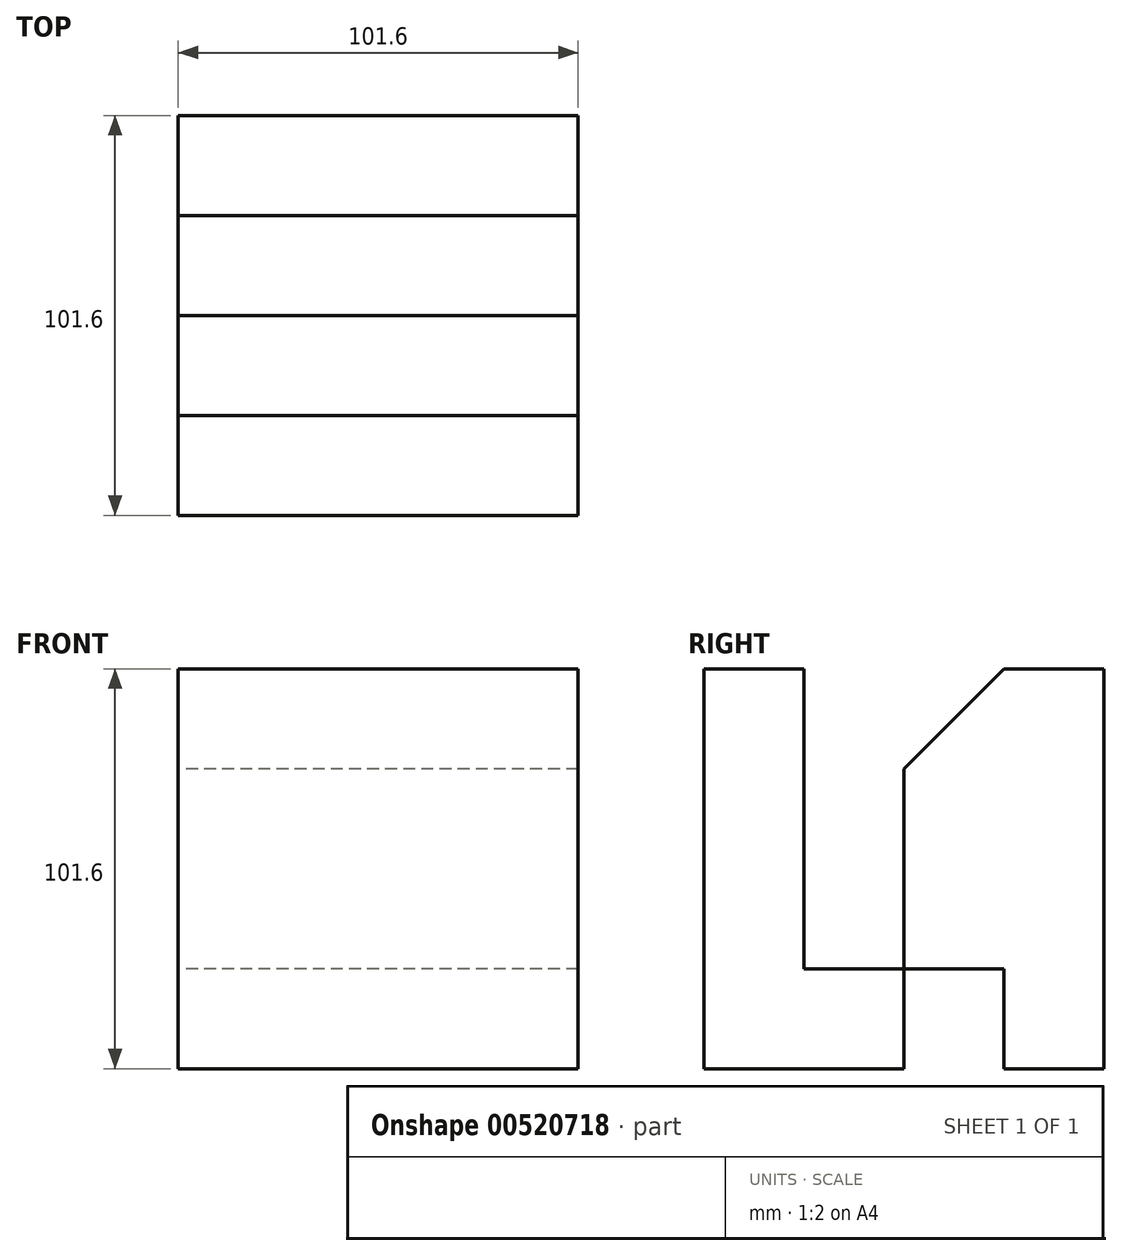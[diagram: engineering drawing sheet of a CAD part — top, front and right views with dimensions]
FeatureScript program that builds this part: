
annotation { "Feature Type Name" : "Feature", "Feature Type Description" : "" }
export const myFeature = defineFeature(function(context is Context, id is Id, definition is map)
    precondition{}
    {
        {
            var Q0;
            Q0=qCreatedBy(makeId("Top.planeOp"),FACE);
            var sketch = newSketch(context, id + "F0", { "sketchPlane" : qUnion([Q0])});
            skLineSegment(sketch, "E0.bottom", {"start": v(-50.8, -50.8) * mm, "end": v(50.8, -50.8) * mm});
            skLineSegment(sketch, "E0.top", {"start": v(-50.8, 50.8) * mm, "end": v(50.8, 50.8) * mm});
            skLineSegment(sketch, "E0.left", {"start": v(-50.8, -50.8) * mm, "end": v(-50.8, 50.8) * mm});
            skLineSegment(sketch, "E0.right", {"start": v(50.8, -50.8) * mm, "end": v(50.8, 50.8) * mm});
            skPoint(sketch, "E0.middle", {"position": v(0, 0) * mm});
            skSolve(sketch);
        }
        {
            var Q0;
            Q0 = qSketchRegion(id + "F0", true);
            extrude(context, id + "F1", {"entities" : qUnion([Q0]), "depth" : 101.6 * mm, "offsetDistance" : 25.4 * mm});
        }
        {
            var Q0;
            Q0=makeQuery(id+"F1.opExtrude","SWEPT_FACE",FACE,{"disambiguationData":[OSD([sQuery(id+"F0.wireOp",EDGE,"E0.left")])]});
            var sketch = newSketch(context, id + "F2", { "sketchPlane" : qUnion([Q0])});
            skLineSegment(sketch, "E1.bottom", {"start": v(-50.8, 101.6) * mm, "end": v(-25.4, 101.6) * mm});
            skLineSegment(sketch, "E1.top", {"start": v(-50.8, 0) * mm, "end": v(-25.4, 0) * mm});
            skLineSegment(sketch, "E1.left", {"start": v(-50.8, 101.6) * mm, "end": v(-50.8, 0) * mm});
            skLineSegment(sketch, "E1.right", {"start": v(-25.4, 101.6) * mm, "end": v(-25.4, 0) * mm});
            skLineSegment(sketch, "E2.bottom", {"start": v(50.8, 101.6) * mm, "end": v(25.4, 101.6) * mm});
            skLineSegment(sketch, "E2.top", {"start": v(50.8, 0) * mm, "end": v(25.4, 0) * mm});
            skLineSegment(sketch, "E2.left", {"start": v(50.8, 101.6) * mm, "end": v(50.8, 0) * mm});
            skLineSegment(sketch, "E2.right", {"start": v(25.4, 101.6) * mm, "end": v(25.4, 0) * mm});
            skLineSegment(sketch, "E3.bottom", {"start": v(-50.8, 101.6) * mm, "end": v(50.8, 101.6) * mm});
            skLineSegment(sketch, "E3.top", {"start": v(-50.8, 76.2) * mm, "end": v(50.8, 76.2) * mm});
            skLineSegment(sketch, "E3.left", {"start": v(-50.8, 101.6) * mm, "end": v(-50.8, 76.2) * mm});
            skLineSegment(sketch, "E3.right", {"start": v(50.8, 101.6) * mm, "end": v(50.8, 76.2) * mm});
            skLineSegment(sketch, "E4.bottom", {"start": v(50.8, 101.6) * mm, "end": v(0, 101.6) * mm});
            skLineSegment(sketch, "E4.top", {"start": v(50.8, 0) * mm, "end": v(0, 0) * mm});
            skLineSegment(sketch, "E4.right", {"start": v(0, 101.6) * mm, "end": v(0, 0) * mm});
            skLineSegment(sketch, "E5.bottom", {"start": v(-50.8, 0) * mm, "end": v(50.8, 0) * mm});
            skLineSegment(sketch, "E5.top", {"start": v(-50.8, 25.4) * mm, "end": v(50.8, 25.4) * mm});
            skLineSegment(sketch, "E5.left", {"start": v(-50.8, 0) * mm, "end": v(-50.8, 25.4) * mm});
            skLineSegment(sketch, "E5.right", {"start": v(50.8, 0) * mm, "end": v(50.8, 25.4) * mm});
            skLineSegment(sketch, "E6.bottom", {"start": v(50.8, 76.2) * mm, "end": v(38.1, 76.2) * mm});
            skLineSegment(sketch, "E6.top", {"start": v(50.8, 50.8) * mm, "end": v(38.1, 50.8) * mm});
            skLineSegment(sketch, "E6.left", {"start": v(50.8, 76.2) * mm, "end": v(50.8, 50.8) * mm});
            skLineSegment(sketch, "E6.right", {"start": v(38.1, 76.2) * mm, "end": v(38.1, 50.8) * mm});
            skLineSegment(sketch, "E7.bottom", {"start": v(-50.8, 76.2) * mm, "end": v(-38.1, 76.2) * mm});
            skLineSegment(sketch, "E7.top", {"start": v(-50.8, 44.75) * mm, "end": v(-38.1, 44.75) * mm});
            skLineSegment(sketch, "E7.left", {"start": v(-50.8, 76.2) * mm, "end": v(-50.8, 44.75) * mm});
            skLineSegment(sketch, "E7.right", {"start": v(-38.1, 76.2) * mm, "end": v(-38.1, 44.75) * mm});
            skSolve(sketch);
        }
        {
            var Q0;
            Q0=makeQuery(id+"F2.imprint","IMPRINT",FACE,{"disambiguationData":[TD([[makeQuery(id+"F2.imprint","IMPRINT",EDGE,{"derivedFrom":sQuery(id+"F2.wireOp",EDGE,"E7.bottom")}),-1.0]])]});
            var Q1;
            Q1=makeQuery(id+"F2.imprint","IMPRINT",FACE,{"disambiguationData":[TD([[makeQuery(id+"F2.imprint","IMPRINT",EDGE,{"derivedFrom":sQuery(id+"F2.wireOp",EDGE,"E6.bottom")}),1.0]])]});
            var Q2;
            {var subQ0=sQuery(id+"F2.wireOp",EDGE,"E5.bottom");var subQ1=sQuery(id+"F2.wireOp",EDGE,"E1.right");var subQ2=makeQuery(id+"F2.imprint","INTERSECT",VERTEX,{"derivedFrom":[subQ1,subQ0]});Q2=makeQuery(id+"F2.imprint","IMPRINT",FACE,{"disambiguationData":[TD([[makeQuery(id+"F2.imprint","IMPRINT",EDGE,{"disambiguationData":[TD([[subQ2,1.0]])],"derivedFrom":subQ1}),1.0]])]});}
            var Q3;
            {var subQ0=sQuery(id+"F2.wireOp",EDGE,"E5.bottom");var subQ1=sQuery(id+"F2.wireOp",EDGE,"E2.right");var subQ2=makeQuery(id+"F2.imprint","INTERSECT",VERTEX,{"derivedFrom":[subQ1,subQ0]});Q3=makeQuery(id+"F2.imprint","IMPRINT",FACE,{"disambiguationData":[TD([[makeQuery(id+"F2.imprint","IMPRINT",EDGE,{"disambiguationData":[TD([[subQ2,1.0]])],"derivedFrom":subQ1}),-1.0]])]});}
            extrude(context, id + "F3", {"entities" : qUnion([Q0, Q1, Q2, Q3]), "operationType" : NewBodyOperationType.REMOVE, "oppositeDirection" : true, "depth" : 101.6 * mm, "offsetDistance" : 25.4 * mm});
        }
        {
            var Q0;
            Q0=makeQuery(id+"F1.opExtrude","SWEPT_FACE",FACE,{"disambiguationData":[OSD([sQuery(id+"F0.wireOp",EDGE,"E0.left")])]});
            var sketch = newSketch(context, id + "F4", { "sketchPlane" : qUnion([Q0])});
            skLineSegment(sketch, "E8.bottom", {"start": v(-50.8, 101.6) * mm, "end": v(0, 101.6) * mm});
            skLineSegment(sketch, "E8.top", {"start": v(-50.8, 76.2) * mm, "end": v(0, 76.2) * mm});
            skLineSegment(sketch, "E8.left", {"start": v(-50.8, 101.6) * mm, "end": v(-50.8, 76.2) * mm});
            skLineSegment(sketch, "E8.right", {"start": v(0, 101.6) * mm, "end": v(0, 76.2) * mm});
            skLineSegment(sketch, "E9.bottom", {"start": v(-50.8, 101.6) * mm, "end": v(-25.4, 101.6) * mm});
            skLineSegment(sketch, "E9.top", {"start": v(-50.8, 76.2) * mm, "end": v(-25.4, 76.2) * mm});
            skLineSegment(sketch, "E9.right", {"start": v(-25.4, 101.6) * mm, "end": v(-25.4, 76.2) * mm});
            skLineSegment(sketch, "E10.bottom", {"start": v(50.8, 101.6) * mm, "end": v(25.4, 101.6) * mm});
            skLineSegment(sketch, "E10.top", {"start": v(50.8, 76.2) * mm, "end": v(25.4, 76.2) * mm});
            skLineSegment(sketch, "E10.left", {"start": v(50.8, 101.6) * mm, "end": v(50.8, 76.2) * mm});
            skLineSegment(sketch, "E10.right", {"start": v(25.4, 101.6) * mm, "end": v(25.4, 76.2) * mm});
            skLineSegment(sketch, "E11", {"start": v(-25.4, 101.6) * mm, "end": v(0, 76.2) * mm});
            skLineSegment(sketch, "E12", {"start": v(25.4, 101.6) * mm, "end": v(0, 76.2) * mm});
            skLineSegment(sketch, "E13", {"start": v(25.4, 101.6) * mm, "end": v(-25.4, 101.6) * mm});
            skSolve(sketch);
        }
        {
            var Q0;
            {var subQ0=sQuery(id+"F4.wireOp",EDGE,"E8.right");Q0=makeQuery(id+"F4.imprint","IMPRINT",FACE,{"disambiguationData":[TD([[makeQuery(id+"F4.imprint","IMPRINT",EDGE,{"derivedFrom":subQ0}),-1.0]])]});}
            var Q1;
            {var subQ0=sQuery(id+"F4.wireOp",EDGE,"E8.right");Q1=makeQuery(id+"F4.imprint","IMPRINT",FACE,{"disambiguationData":[TD([[makeQuery(id+"F4.imprint","IMPRINT",EDGE,{"derivedFrom":subQ0}),1.0]])]});}
            extrude(context, id + "F5", {"entities" : qUnion([Q0, Q1]), "operationType" : NewBodyOperationType.REMOVE, "oppositeDirection" : true, "depth" : 101.6 * mm, "offsetDistance" : 25.4 * mm});
        }
    });
